# Revit family: Kohler Strayt 37337A-4-CP Family
name_source: partatom
category: Plumbing Fixtures
revit_build: Autodesk Revit 2018 (Build: 20170223_1515(x64)
units: mm (PartAtom-declared; Revit-internal decimal feet)

## family parameters
Cut with Voids When Loaded = No
Host = Face
Part Type = Normal
Room Calculation Point = No
Round Connector Dimension = Use Diameter
Shared = No

## types (1)
- Kohler 37337A-4-CP
    Default Elevation = 1219 mm
    Description = STRAYT DECK MOUNT BATH & SHOWER FAUCET
    Disclamer = Although care has been taken to ensure, to the best of our knowledge, that all data and information contained herein is accurate
to the extent that it relates to either matters of fact or accepted practice at the time of issue. MDFC (Pty) Ltd assumes no responsibility for
any errors in, or misinterpretation of, such data and/ or information or any loss or damage arising from, or related to its use.
    Faucet Height = 260 mm
    Faucet Width = 177 mm
    Hand Shower Lenght = 28 mm
    Manufacturer = Kohler CO
    Material = Faucets
    Model = 37337A-4-CP
    Telephone = 011 050 9000
    URL = http://www.africa.kohler.com
    Valve Height = 79 mm

## geometry (parser evidence)
native form markers: Sweep x3
no freeform markers — native parametric forms only
